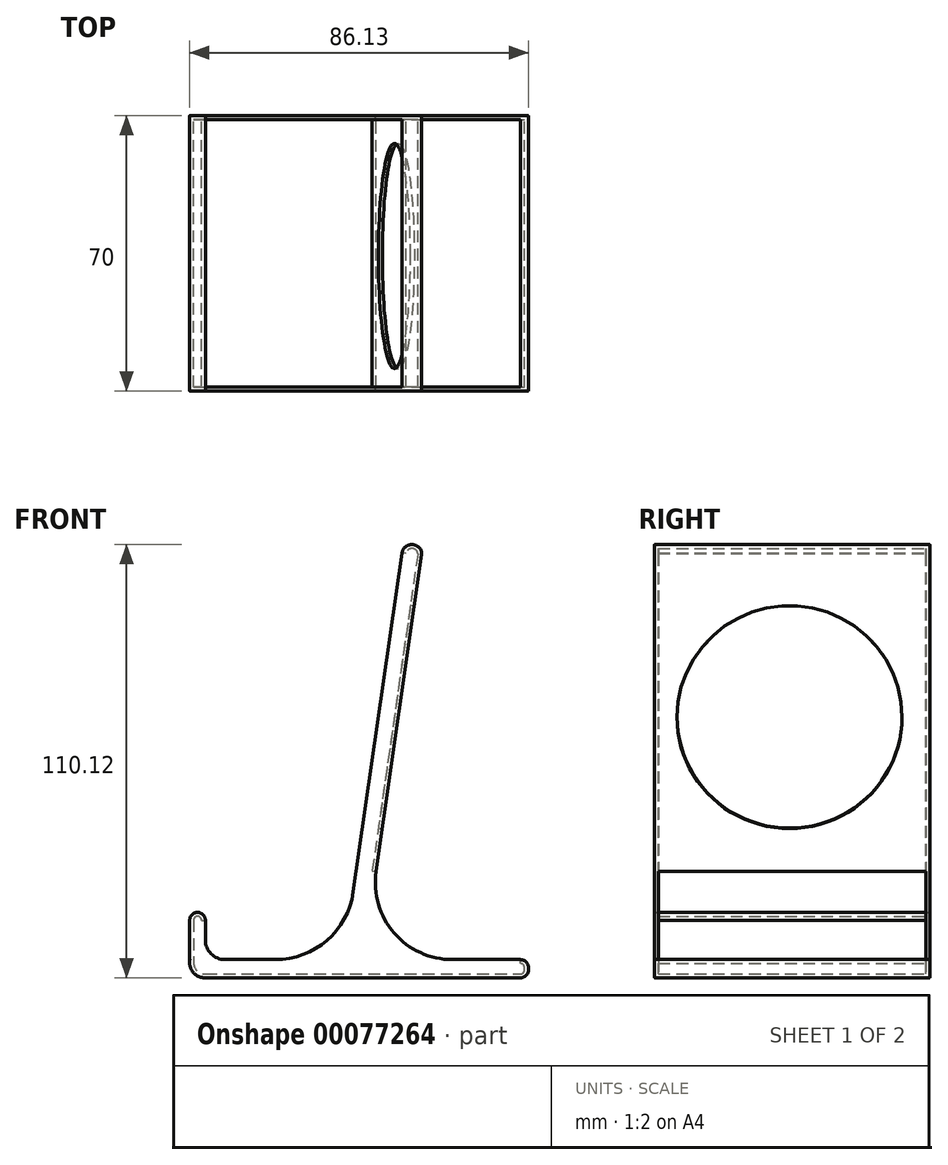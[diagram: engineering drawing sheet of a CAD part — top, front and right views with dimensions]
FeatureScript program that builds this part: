
annotation { "Feature Type Name" : "Feature", "Feature Type Description" : "" }
export const myFeature = defineFeature(function(context is Context, id is Id, definition is map)
    precondition{}
    {
        {
            var Q0;
            Q0=qCreatedBy(makeId("Front.planeOp"),FACE);
            var sketch = newSketch(context, id + "F0", { "sketchPlane" : qUnion([Q0])});
            skLineSegment(sketch, "E0.bottom", {"start": v(-26.37, 5.3) * mm, "end": v(-13.6, 5.3) * mm});
            skLineSegment(sketch, "E0.top", {"start": v(-31.37, 0.64) * mm, "end": v(48.63, 0.64) * mm});
            skLineSegment(sketch, "E0.right", {"start": v(50.71, 3.22) * mm, "end": v(50.71, 2.72) * mm});
            skPoint(sketch, "E1.visualSharp", {"position": v(50.71, 5.3) * mm});
            skArc(sketch, "E1.filletArc", {"start": v(50.71, 3.22) * mm, "mid": v(50.1, 4.7) * mm, "end": v(48.63, 5.3) * mm});
            skPoint(sketch, "E2.visualSharp", {"position": v(50.71, 0.64) * mm});
            skArc(sketch, "E2.filletArc", {"start": v(48.63, 0.64) * mm, "mid": v(50.1, 1.25) * mm, "end": v(50.71, 2.72) * mm});
            skArc(sketch, "E3", {"start": v(-31.37, 0.64) * mm, "mid": v(-34.44, 2.05) * mm, "end": v(-35.37, 5.3) * mm});
            skLineSegment(sketch, "E4", {"start": v(-35.37, 5.3) * mm, "end": v(-35.37, 15.3) * mm});
            skLineSegment(sketch, "E5", {"start": v(-31.37, 10.3) * mm, "end": v(-31.37, 15.3) * mm});
            skPoint(sketch, "E6.visualSharp", {"position": v(-31.37, 5.3) * mm});
            skArc(sketch, "E6.filletArc", {"start": v(-31.37, 10.3) * mm, "mid": v(-29.9, 6.77) * mm, "end": v(-26.37, 5.3) * mm});
            skPoint(sketch, "E7.visualSharp", {"position": v(-47.16, 42.3) * mm});
            skArc(sketch, "E8", {"start": v(1.2, 30.47) * mm, "mid": v(1.7, 30.69) * mm, "end": v(2.18, 30.91) * mm});
            skLineSegment(sketch, "E9", {"start": v(12, 27.69) * mm, "end": v(10.54, 17.56) * mm});
            skLineSegment(sketch, "E10", {"start": v(10.54, 17.56) * mm, "end": v(23.57, 108.18) * mm});
            skLineSegment(sketch, "E11", {"start": v(17.58, 101.65) * mm, "end": v(18.58, 108.57) * mm});
            skArc(sketch, "E12", {"start": v(18.58, 108.57) * mm, "mid": v(20.68, 110.73) * mm, "end": v(23.37, 109.39) * mm});
            skPoint(sketch, "E13.visualSharp", {"position": v(23.63, 108.57) * mm});
            skArc(sketch, "E13.filletArc", {"start": v(23.57, 108.18) * mm, "mid": v(23.56, 108.8) * mm, "end": v(23.37, 109.39) * mm});
            skLineSegment(sketch, "E14", {"start": v(9.04, 42.26) * mm, "end": v(6.19, 22.46) * mm});
            skLineSegment(sketch, "E15.trimOffspring", {"start": v(31.38, 5.3) * mm, "end": v(48.63, 5.3) * mm});
            skPoint(sketch, "E16.visualSharp", {"position": v(8.77, 5.3) * mm});
            skArc(sketch, "E16.filletArc", {"start": v(12, 27.69) * mm, "mid": v(16.58, 12.07) * mm, "end": v(31.38, 5.3) * mm});
            skPoint(sketch, "E17.visualSharp", {"position": v(3.72, 5.3) * mm});
            skArc(sketch, "E17.filletArc", {"start": v(-13.6, 5.3) * mm, "mid": v(-0.51, 10.2) * mm, "end": v(6.19, 22.46) * mm});
            skLineSegment(sketch, "E18", {"start": v(17.58, 101.65) * mm, "end": v(9.04, 42.26) * mm});
            skArc(sketch, "E19", {"start": v(-35.37, 15.3) * mm, "mid": v(-33.37, 17.3) * mm, "end": v(-31.37, 15.3) * mm});
            skPoint(sketch, "E20", {"position": v(24.71, 0.64) * mm});
            skSolve(sketch);
        }
        {
            var Q0;
            Q0=makeQuery(id+"F0.imprint","IMPRINT",FACE,{"disambiguationData":[TD([[makeQuery(id+"F0.imprint","IMPRINT",EDGE,{"derivedFrom":sQuery(id+"F0.wireOp",EDGE,"E0.bottom")}),-1.0]])]});
            extrude(context, id + "F1", {"entities" : qUnion([Q0]), "depth" : 70 * mm});
        }
        {
            var Q0;
            Q0=makeQuery(id+"F1.opExtrude","CAP_FACE",FACE,{"disambiguationData":[OSD([sQuery(id+"F0.wireOp",EDGE,"E0.bottom"),sQuery(id+"F0.wireOp",EDGE,"E0.top"),sQuery(id+"F0.wireOp",EDGE,"E0.right"),sQuery(id+"F0.wireOp",EDGE,"E1.filletArc"),sQuery(id+"F0.wireOp",EDGE,"E2.filletArc"),sQuery(id+"F0.wireOp",EDGE,"E3"),sQuery(id+"F0.wireOp",EDGE,"E4"),sQuery(id+"F0.wireOp",EDGE,"E5"),sQuery(id+"F0.wireOp",EDGE,"E6.filletArc"),sQuery(id+"F0.wireOp",EDGE,"dc141114-140d-4cd2-be7c-44f066d90e01"),sQuery(id+"F0.wireOp",EDGE,"WlStoxGS-s4TI-MyU9-pMey-WDQfSKRiyZ1e"),sQuery(id+"F0.wireOp",EDGE,"zgLxOgAg-QXhc-Ya1E-6De7-TgZCOx7TSNqv"),sQuery(id+"F0.wireOp",EDGE,"E7.filletArc"),sQuery(id+"F0.wireOp",EDGE,"hKBkdubu-fKdq-YkXF-CLfD-YmTfWPYBa9Az"),sQuery(id+"F0.wireOp",EDGE,"86bc8ff0-6799-4a6b-88f5-181a7f902f32.0"),sQuery(id+"F0.wireOp",EDGE,"E8"),sQuery(id+"F0.wireOp",EDGE,"E9"),sQuery(id+"F0.wireOp",EDGE,"E10"),sQuery(id+"F0.wireOp",EDGE,"E11"),sQuery(id+"F0.wireOp",EDGE,"E12"),sQuery(id+"F0.wireOp",EDGE,"E13.filletArc"),sQuery(id+"F0.wireOp",EDGE,"E14"),sQuery(id+"F0.wireOp",EDGE,"E15.trimOffspring"),sQuery(id+"F0.wireOp",EDGE,"E16.filletArc"),sQuery(id+"F0.wireOp",EDGE,"E17.filletArc"),sQuery(id+"F0.wireOp",EDGE,"s00ZNOpZ-fLz4-HHjH-Khz0-f1FcPi00xW1T"),sQuery(id+"F0.wireOp",EDGE,"B8UtTqyL-tXw6-W4UG-K7x7-I18TURwFkFkb"),sQuery(id+"F0.wireOp",EDGE,"75321f87-7671-4821-88a1-bef03739b513.filletArc")])],"isStart":false});
            var Q1;
            Q1=makeQuery(id+"F1.opExtrude","CAP_FACE",FACE,{"disambiguationData":[OSD([sQuery(id+"F0.wireOp",EDGE,"E0.bottom"),sQuery(id+"F0.wireOp",EDGE,"E0.top"),sQuery(id+"F0.wireOp",EDGE,"E0.right"),sQuery(id+"F0.wireOp",EDGE,"E1.filletArc"),sQuery(id+"F0.wireOp",EDGE,"E2.filletArc"),sQuery(id+"F0.wireOp",EDGE,"E3"),sQuery(id+"F0.wireOp",EDGE,"E4"),sQuery(id+"F0.wireOp",EDGE,"E5"),sQuery(id+"F0.wireOp",EDGE,"E6.filletArc"),sQuery(id+"F0.wireOp",EDGE,"dc141114-140d-4cd2-be7c-44f066d90e01"),sQuery(id+"F0.wireOp",EDGE,"WlStoxGS-s4TI-MyU9-pMey-WDQfSKRiyZ1e"),sQuery(id+"F0.wireOp",EDGE,"zgLxOgAg-QXhc-Ya1E-6De7-TgZCOx7TSNqv"),sQuery(id+"F0.wireOp",EDGE,"E7.filletArc"),sQuery(id+"F0.wireOp",EDGE,"hKBkdubu-fKdq-YkXF-CLfD-YmTfWPYBa9Az"),sQuery(id+"F0.wireOp",EDGE,"86bc8ff0-6799-4a6b-88f5-181a7f902f32.0"),sQuery(id+"F0.wireOp",EDGE,"E8"),sQuery(id+"F0.wireOp",EDGE,"E9"),sQuery(id+"F0.wireOp",EDGE,"E10"),sQuery(id+"F0.wireOp",EDGE,"E11"),sQuery(id+"F0.wireOp",EDGE,"E12"),sQuery(id+"F0.wireOp",EDGE,"E13.filletArc"),sQuery(id+"F0.wireOp",EDGE,"E14"),sQuery(id+"F0.wireOp",EDGE,"E15.trimOffspring"),sQuery(id+"F0.wireOp",EDGE,"E16.filletArc"),sQuery(id+"F0.wireOp",EDGE,"E17.filletArc"),sQuery(id+"F0.wireOp",EDGE,"s00ZNOpZ-fLz4-HHjH-Khz0-f1FcPi00xW1T"),sQuery(id+"F0.wireOp",EDGE,"B8UtTqyL-tXw6-W4UG-K7x7-I18TURwFkFkb"),sQuery(id+"F0.wireOp",EDGE,"75321f87-7671-4821-88a1-bef03739b513.filletArc")])],"isStart":true});
            fillet(context, id + "F2", {"entities" : qUnion([Q0, Q1]), "radius" : 0.1 * mm, "tangentPropagation" : true, "allowEdgeOverflow" : false});
        }
        {
            var Q0;
            Q0=makeQuery(id+"F1.opExtrude","SWEPT_FACE",FACE,{"disambiguationData":[OSD([sQuery(id+"F0.wireOp",EDGE,"E11"),sQuery(id+"F0.wireOp",EDGE,"E14"),sQuery(id+"F0.wireOp",EDGE,"E18")])]});
            var Q1;
            Q1=makeQuery(id+"F1.opExtrude","SWEPT_FACE",FACE,{"disambiguationData":[OSD([sQuery(id+"F0.wireOp",EDGE,"E0.bottom")])]});
            var Q2;
            Q2=makeQuery(id+"F1.opExtrude","SWEPT_FACE",FACE,{"disambiguationData":[OSD([sQuery(id+"F0.wireOp",EDGE,"E17.filletArc")])]});
            var Q3;
            Q3=makeQuery(id+"F1.opExtrude","SWEPT_FACE",FACE,{"disambiguationData":[OSD([sQuery(id+"F0.wireOp",EDGE,"E5")])]});
            var Q4;
            Q4=makeQuery(id+"F1.opExtrude","SWEPT_FACE",FACE,{"disambiguationData":[OSD([sQuery(id+"F0.wireOp",EDGE,"E6.filletArc")])]});
            var Q5;
            Q5=makeQuery(id+"F1.opExtrude","SWEPT_FACE",FACE,{"disambiguationData":[OSD([sQuery(id+"F0.wireOp",EDGE,"E16.filletArc")])]});
            var Q6;
            Q6=makeQuery(id+"F1.opExtrude","SWEPT_FACE",FACE,{"disambiguationData":[OSD([sQuery(id+"F0.wireOp",EDGE,"E15.trimOffspring")])]});
            shell(context, id + "F3", {"entities" : qUnion([Q0, Q1, Q2, Q3, Q4, Q5, Q6]), "thickness" : 1 * mm});
        }
        {
            var Q0;
            Q0=makeQuery(id+"F1.opExtrude","SWEPT_FACE",FACE,{"disambiguationData":[OSD([sQuery(id+"F0.wireOp",EDGE,"E10")])]});
            var sketch = newSketch(context, id + "F4", { "sketchPlane" : qUnion([Q0])});
            skCircle(sketch, "E21", {"center": v(-35.67, 68.73) * mm, "radius": 28.6 * mm});
            skSolve(sketch);
        }
        {
            var Q0;
            Q0=makeQuery(id+"F4.imprint","IMPRINT",FACE,{"disambiguationData":[TD([[makeQuery(id+"F4.imprint","IMPRINT",EDGE,{"derivedFrom":sQuery(id+"F4.wireOp",EDGE,"E21")}),1.0]])]});
            extrude(context, id + "F5", {"entities" : qUnion([Q0]), "operationType" : NewBodyOperationType.REMOVE, "oppositeDirection" : true, "depth" : 25 * mm});
        }
    });
